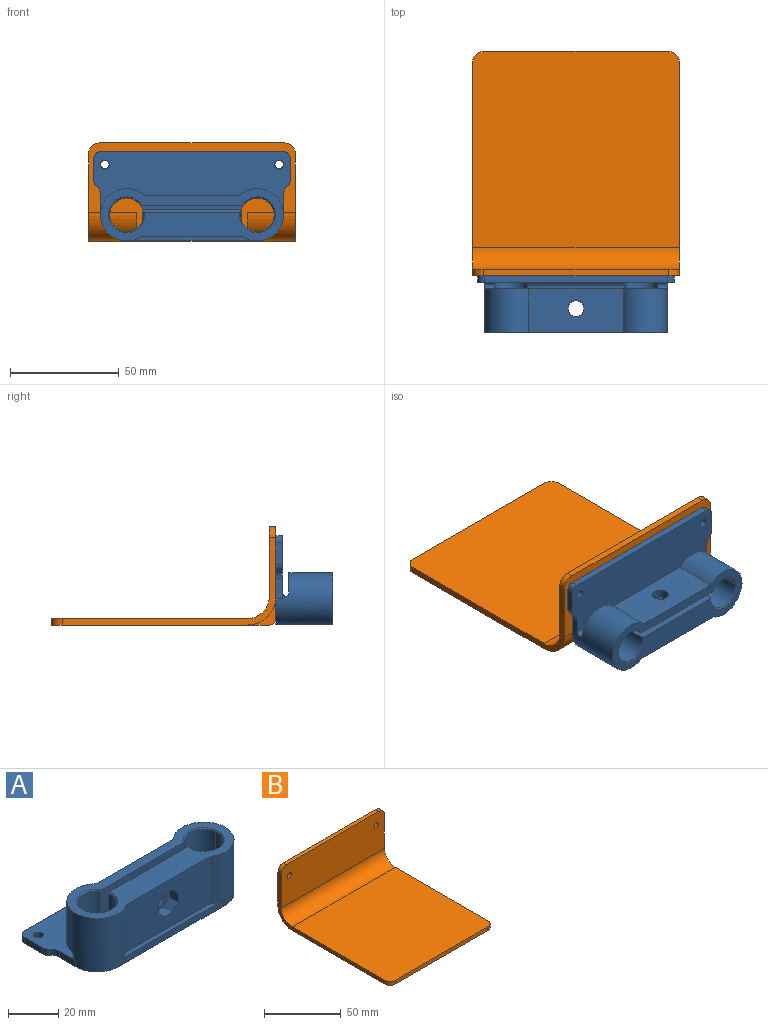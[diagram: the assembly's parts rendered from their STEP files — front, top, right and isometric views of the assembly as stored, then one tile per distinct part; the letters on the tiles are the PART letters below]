
ASSEMBLY  parts=2 mates=1
PART A: 46 faces, bbox 90x41x26 mm
  f0: plane 46.87x23mm, normal (0,-1,0), area 977.8mm2, adj f2,f3,f10,f14,f15,f16,f17,f18
  f1: cylinder r=3.67mm len=7.35mm, axis (0,1,0), area 139.6mm2, adj f8,f22
  f2: cylinder r=12mm len=26mm, axis (0,0,1), area 1215.3mm2, adj f0,f9,f10,f23,f25,f26,f32,f33
  f3: cylinder r=12mm len=26mm, axis (0,0,1), area 1215.3mm2, adj f0,f9,f10,f23,f24,f25,f32,f33
  f4: cylinder r=7.7mm len=25mm, axis (0,0,1), area 1076.4mm2, adj f5,f8,f13,f23,f34,f36,f37,f39
  f5: plane 47.18x20.01mm, normal (0,-1,0), area 900.7mm2, adj f4,f7,f10,f11,f12,f13,f34
  f6: cylinder r=7.7mm len=25mm, axis (0,0,1), area 714.5mm2, adj f7,f8,f12,f23,f35,f38,f39
  f7: cylinder r=7.7mm len=21mm, axis (0,0,1), area 361.9mm2, adj f5,f6,f12,f34,f38
  f8: plane 44.73x21.5mm, normal (0,1,0), area 919mm2, adj f1,f4,f6,f10,f12,f13,f39
  f9: plane 43.34x20mm, normal (0,1,0), area 824.4mm2, adj f2,f3,f10,f11,f34
  f10: plane 84x24mm, normal (0,0,1), area 1061.6mm2, adj f0,f2,f3,f5,f8,f9,f12,f13
  f11: cylinder r=3.67mm len=7.35mm, axis (0,1,0), area 101.1mm2, adj f5,f9
  f12: cone r=8.2mm half-angle=45deg, axis (0,0,1), area 32.8mm2, adj f5,f6,f7,f8,f10
  f13: cone r=7.7mm half-angle=45deg, axis (0,0,1), area 32.8mm2, adj f4,f5,f8,f10
  f14: plane 5x4.56mm, normal (0,0,-1), area 22.8mm2, adj f0,f15,f21,f22
  f15: plane 5x3.22mm, normal (0.71,0,-0.71), area 22.8mm2, adj f0,f14,f16,f22
  f16: plane 5x4.56mm, normal (1,0,0), area 22.8mm2, adj f0,f15,f17,f22
  f17: plane 5x3.22mm, normal (0.71,0,0.71), area 22.8mm2, adj f0,f16,f18,f22
  f18: plane 5x4.56mm, normal (0,0,1), area 22.8mm2, adj f0,f17,f19,f22
  f19: plane 5x3.22mm, normal (-0.71,0,0.71), area 22.8mm2, adj f0,f18,f20,f22
  f20: plane 5x4.56mm, normal (-1,0,0), area 22.8mm2, adj f0,f19,f21,f22
  f21: plane 5x3.22mm, normal (-0.71,0,-0.71), area 22.8mm2, adj f0,f14,f20,f22
  f22: plane 11x11mm, normal (0,-1,0), area 57.8mm2, adj f1,f14,f15,f16,f17,f18,f19,f20
  f23: plane 90x29mm, normal (0,0,1), area 2183.4mm2, adj f2,f3,f4,f6,f24,f26,f27,f28
  f24: plane 9.26x3mm, normal (1,0,0), area 27.8mm2, adj f3,f23,f32,f45
  f25: plane 60x3mm, normal (0,-1,0), area 180mm2, adj f2,f3,f32,f33
  f26: plane 9.26x3mm, normal (-1,0,0), area 27.8mm2, adj f2,f23,f32,f44
  f27: plane 10.5x3mm, normal (-1,0,0), area 31.5mm2, adj f23,f32,f40,f41
  f28: plane 84x3mm, normal (0,1,0), area 252mm2, adj f23,f32,f41,f42
  f29: cylinder r=2mm len=4mm, axis (0,0,1), area 37.7mm2, adj f23,f32
  f30: cylinder r=2mm len=4mm, axis (0,0,1), area 37.7mm2, adj f23,f32
  f31: plane 10.5x3mm, normal (1,0,0), area 31.5mm2, adj f23,f32,f42,f43
  f32: plane 90x41mm, normal (0,0,-1), area 3028.6mm2, adj f2,f3,f24,f25,f26,f27,f28,f29
  f33: plane 60x1.95mm, normal (0,0,1), area 99.9mm2, adj f0,f2,f3,f25
  f34: plane 83.41x9.36mm, normal (0,0,-1), area 380.3mm2, adj f2,f3,f4,f5,f7,f9,f37,f38
  f35: cone r=7.7mm half-angle=45deg, axis (0,0,-1), area 35.3mm2, adj f6,f32
  f36: cone r=8.2mm half-angle=45deg, axis (0,0,-1), area 35.3mm2, adj f4,f32
  f37: cylinder r=1.5mm len=4.71mm, axis (1,0,0), area 20.6mm2, adj f2,f4,f23,f34
  f38: cylinder r=1.5mm len=4.71mm, axis (-1,0,0), area 20.6mm2, adj f3,f6,f7,f23,f34
  f39: cylinder r=1.5mm len=45.44mm, axis (-1,0,0), area 105.9mm2, adj f4,f6,f8,f23
  f40: cylinder r=3mm len=3mm, axis (0,0,1), area 8.1mm2, adj f23,f27,f32,f44
  f41: cylinder r=3mm len=3mm, axis (0,0,-1), area 14.1mm2, adj f23,f27,f28,f32
  f42: cylinder r=3mm len=3mm, axis (0,0,1), area 14.1mm2, adj f23,f28,f31,f32
  f43: cylinder r=3mm len=3mm, axis (0,0,-1), area 8.1mm2, adj f23,f31,f32,f45
  f44: cylinder r=5mm len=3.9mm, axis (0,0,1), area 13.4mm2, adj f23,f26,f32,f40
  f45: cylinder r=5mm len=3.9mm, axis (0,0,-1), area 13.4mm2, adj f23,f24,f32,f43
PART B: 28 faces, bbox 94.8x103x45 mm
  f0: cylinder r=13mm len=21mm, axis (1,0,0), area 428.8mm2, adj f5,f10,f18,f22
  f1: cylinder r=13mm len=21.92mm, axis (1,0,0), area 447.6mm2, adj f5,f6,f10,f19
  f2: cylinder r=13mm len=21mm, axis (1,0,0), area 428.8mm2, adj f5,f10,f17,f20
  f3: plane 94.83x32mm, normal (0,-1,0), area 2998.8mm2, adj f4,f6,f7,f8,f9,f13,f15,f16
  f4: plane 98x40mm, normal (-1,0,0), area 390.2mm2, adj f3,f5,f10,f11,f13,f14,f16,f26
  f5: plane 100x94.83mm, normal (0,0,-1), area 8614.4mm2, adj f0,f1,f2,f4,f6,f12,f14,f17
  f6: plane 98x40mm, normal (1,0,0), area 390.2mm2, adj f1,f3,f5,f10,f11,f13,f15,f27
  f7: cylinder r=2mm len=4mm, axis (0,1,0), area 37.7mm2, adj f3,f10
  f8: cylinder r=2mm len=4mm, axis (0,1,0), area 37.7mm2, adj f3,f10
  f9: plane 84.83x3mm, normal (0,0,1), area 254.5mm2, adj f3,f10,f15,f16
  f10: plane 94.83x42mm, normal (0,1,0), area 3088.8mm2, adj f0,f1,f2,f4,f6,f7,f8,f9
  f11: plane 94.83x90mm, normal (0,0,1), area 8524.4mm2, adj f4,f6,f12,f13,f26,f27
  f12: plane 84.83x3mm, normal (0,-1,0), area 254.5mm2, adj f5,f11,f26,f27
  f13: cylinder r=10mm len=94.83mm, axis (-1,0,0), area 1489.7mm2, adj f3,f4,f6,f11
  f14: cylinder r=13mm len=21.92mm, axis (1,0,0), area 447.6mm2, adj f4,f5,f10,f21
  f15: cylinder r=5mm len=5mm, axis (0,1,0), area 23.6mm2, adj f3,f6,f9,f10
  f16: cylinder r=5mm len=5mm, axis (0,-1,0), area 23.6mm2, adj f3,f4,f9,f10
  f17: plane 13x13mm, normal (1,0,0), area 34.3mm2, adj f2,f5,f10,f25
  f18: plane 13x13mm, normal (-1,0,0), area 34.3mm2, adj f0,f5,f10,f25
  f19: plane 13x13mm, normal (1,0,0), area 34.3mm2, adj f1,f5,f10,f24
  f20: plane 13x13mm, normal (-1,0,0), area 34.3mm2, adj f2,f5,f10,f24
  f21: plane 13x13mm, normal (-1,0,0), area 34.3mm2, adj f5,f10,f14,f23
  f22: plane 13x13mm, normal (1,0,0), area 34.3mm2, adj f0,f5,f10,f23
  f23: cylinder r=3mm len=3mm, axis (1,0,0), area 14.1mm2, adj f5,f10,f21,f22
  f24: cylinder r=3mm len=3mm, axis (-1,0,0), area 14.1mm2, adj f5,f10,f19,f20
  f25: cylinder r=3mm len=3mm, axis (-1,0,0), area 14.1mm2, adj f5,f10,f17,f18
  f26: cylinder r=5mm len=5mm, axis (0,0,1), area 23.6mm2, adj f4,f5,f11,f12
  f27: cylinder r=5mm len=5mm, axis (0,0,-1), area 23.6mm2, adj f5,f6,f11,f12
PLACE A rot(axis=(1,0,0),90deg) t=(-103.31,88.85,19.98)mm
PLACE B rot(axis=(0,0,1),180deg) t=(-103.31,56.94,48.19)mm
MATE planar B.f10 <-> A.f32  axis (0,-1,0) through (-103.31,56.94,41.22)mm
